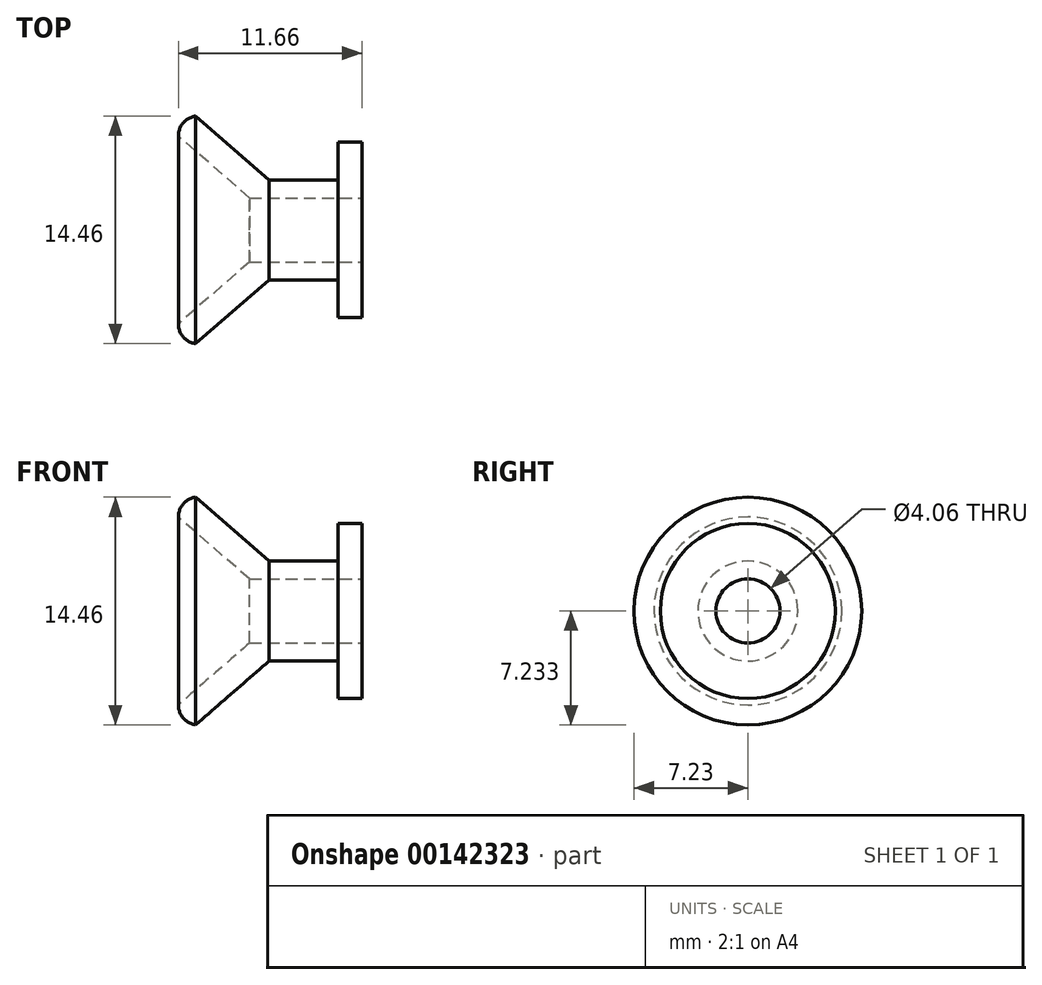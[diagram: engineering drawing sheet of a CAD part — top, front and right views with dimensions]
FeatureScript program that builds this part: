
annotation { "Feature Type Name" : "Feature", "Feature Type Description" : "" }
export const myFeature = defineFeature(function(context is Context, id is Id, definition is map)
    precondition{}
    {
        {
            var Q0;
            Q0=qCreatedBy(makeId("Front.planeOp"),FACE);
            var sketch = newSketch(context, id + "F0", { "sketchPlane" : qUnion([Q0])});
            skLineSegment(sketch, "E0", {"start": v(-131.71, 25.3) * mm, "end": v(-157.11, 25.3) * mm, "construction": true});
            skLineSegment(sketch, "E1", {"start": v(-131.71, 23.27) * mm, "end": v(-131.71, 19.74) * mm});
            skLineSegment(sketch, "E2", {"start": v(-131.71, 19.74) * mm, "end": v(-133.24, 19.74) * mm});
            skLineSegment(sketch, "E3", {"start": v(-133.24, 19.74) * mm, "end": v(-133.24, 22.13) * mm});
            skLineSegment(sketch, "E4", {"start": v(-133.24, 22.13) * mm, "end": v(-137.6, 22.13) * mm});
            skLineSegment(sketch, "E5", {"start": v(-137.6, 22.13) * mm, "end": v(-142.27, 18.07) * mm});
            skLineSegment(sketch, "E6", {"start": v(-131.71, 23.27) * mm, "end": v(-138.85, 23.27) * mm});
            skLineSegment(sketch, "E7", {"start": v(-138.85, 23.27) * mm, "end": v(-143.37, 19.34) * mm});
            skLineSegment(sketch, "E8", {"start": v(-142.27, 18.07) * mm, "end": v(-143.37, 19.34) * mm, "construction": true});
            skArc(sketch, "E9", {"start": v(-143.37, 19.34) * mm, "mid": v(-143.06, 18.5) * mm, "end": v(-142.27, 18.07) * mm});
            skSolve(sketch);
        }
        {
            var Q0;
            Q0=makeQuery(id+"F0.imprint","IMPRINT",FACE,{"disambiguationData":[TD([[makeQuery(id+"F0.imprint","IMPRINT",EDGE,{"derivedFrom":sQuery(id+"F0.wireOp",EDGE,"E1")}),-1.0]])]});
            var Q1;
            Q1=sQuery(id+"F0.wireOp",EDGE,"E1");
            var Q2;
            Q2=sQuery(id+"F0.wireOp",EDGE,"E2");
            var Q3;
            Q3=sQuery(id+"F0.wireOp",EDGE,"E3");
            var Q4;
            Q4=sQuery(id+"F0.wireOp",EDGE,"E4");
            var Q5;
            Q5=sQuery(id+"F0.wireOp",EDGE,"E5");
            var Q6;
            Q6=sQuery(id+"F0.wireOp",EDGE,"E6");
            var Q7;
            Q7=sQuery(id+"F0.wireOp",EDGE,"E7");
            var Q8;
            Q8=sQuery(id+"F0.wireOp",EDGE,"E9");
            var Q9;
            Q9=sQuery(id+"F0.wireOp",EDGE,"E0");
            revolve(context, id + "F1", {"entities" : qUnion([Q0]), "surfaceEntities" : qUnion([Q1, Q2, Q3, Q4, Q5, Q6, Q7, Q8]), "axis" : qUnion([Q9]), "revolveType" : RevolveType.FULL});
        }
    });
